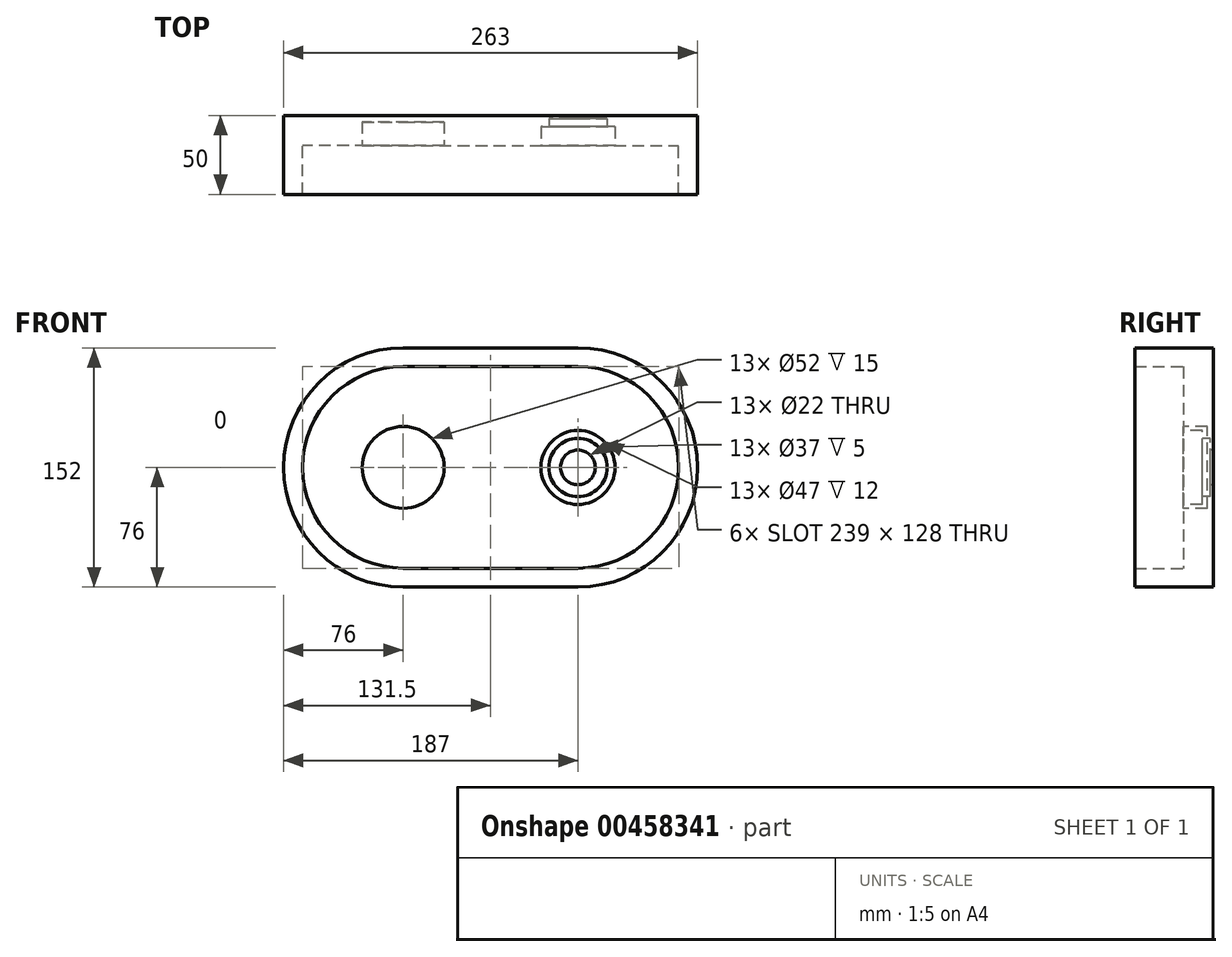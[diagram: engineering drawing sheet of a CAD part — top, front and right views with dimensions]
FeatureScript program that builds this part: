
annotation { "Feature Type Name" : "Feature", "Feature Type Description" : "" }
export const myFeature = defineFeature(function(context is Context, id is Id, definition is map)
    precondition{}
    {
        {
            var Q0;
            Q0=qCreatedBy(makeId("Front.planeOp"),FACE);
            var sketch = newSketch(context, id + "F0", { "sketchPlane" : qUnion([Q0])});
            skArc(sketch, "E0", {"start": v(0, 76) * mm, "mid": v(-76, 0) * mm, "end": v(0, -76) * mm});
            skArc(sketch, "E1", {"start": v(111, -76) * mm, "mid": v(187, 0) * mm, "end": v(111, 76) * mm});
            skLineSegment(sketch, "E2", {"start": v(0, 76) * mm, "end": v(111, 76) * mm});
            skLineSegment(sketch, "E3", {"start": v(0, -76) * mm, "end": v(111, -76) * mm});
            skSolve(sketch);
        }
        {
            var Q0;
            Q0=qCreatedBy(makeId("Front.planeOp"),FACE);
            cPlane(context, id + "F1", {"entities" : qUnion([Q0]), "cplaneType" : CPlaneType.OFFSET, "offset" : 19 * mm, "width" : 150 * mm, "height" : 150 * mm});
        }
        {
            var Q0;
            Q0=makeQuery(id+"F0.imprint","IMPRINT",FACE,{"disambiguationData":[TD([[makeQuery(id+"F0.imprint","IMPRINT",EDGE,{"derivedFrom":sQuery(id+"F0.wireOp",EDGE,"E0")}),1.0]])]});
            extrude(context, id + "F2", {"entities" : qUnion([Q0]), "depth" : 50 * mm, "offsetDistance" : 25 * mm});
        }
        {
            var Q0;
            Q0=qCreatedBy(id+"F1.planeOp",FACE);
            var sketch = newSketch(context, id + "F3", { "sketchPlane" : qUnion([Q0])});
            skArc(sketch, "E4", {"start": v(0, 64) * mm, "mid": v(-64, 0) * mm, "end": v(0, -64) * mm});
            skArc(sketch, "E5", {"start": v(111, -64) * mm, "mid": v(175, 0) * mm, "end": v(111, 64) * mm});
            skLineSegment(sketch, "E6", {"start": v(0, 64) * mm, "end": v(111, 64) * mm});
            skLineSegment(sketch, "E7", {"start": v(0, -64) * mm, "end": v(111, -64) * mm});
            skCircle(sketch, "E8", {"center": v(0, 0) * mm, "radius": 26 * mm});
            skSolve(sketch);
        }
        {
            var Q0;
            Q0 = qSketchRegion(id + "F3", true);
            extrude(context, id + "F4", {"entities" : qUnion([Q0]), "operationType" : NewBodyOperationType.REMOVE, "depth" : 100 * mm, "offsetDistance" : 25 * mm});
        }
        {
            var Q0;
            Q0=makeQuery(id+"F4.boolean.opBoolean","SPLIT",FACE,{"disambiguationData":[TD([makeQuery(id+"F4.opExtrude","SWEPT_FACE",FACE,{"disambiguationData":[OSD([sQuery(id+"F3.wireOp",EDGE,"E8")])]})])],"derivedFrom":makeQuery(id+"F2.opExtrude","CAP_FACE",FACE,{"disambiguationData":[OSD([sQuery(id+"F0.wireOp",EDGE,"E0"),sQuery(id+"F0.wireOp",EDGE,"E1"),sQuery(id+"F0.wireOp",EDGE,"E2"),sQuery(id+"F0.wireOp",EDGE,"E3")])],"isStart":false})});
            extrude(context, id + "F5", {"entities" : qUnion([Q0]), "operationType" : NewBodyOperationType.REMOVE, "oppositeDirection" : true, "depth" : 46 * mm, "offsetDistance" : 25 * mm});
        }
        {
            var Q0;
            Q0=qCreatedBy(makeId("Right.planeOp"),FACE);
            cPlane(context, id + "F6", {"entities" : qUnion([Q0]), "cplaneType" : CPlaneType.OFFSET, "offset" : 111 * mm, "width" : 150 * mm, "height" : 150 * mm});
        }
        {
            var Q0;
            Q0=qCreatedBy(id+"F6.planeOp",FACE);
            var sketch = newSketch(context, id + "F7", { "sketchPlane" : qUnion([Q0])});
            skLineSegment(sketch, "E9.bottom", {"start": v(0, 0) * mm, "end": v(-19, 0) * mm});
            skLineSegment(sketch, "E9.top", {"start": v(0, 11) * mm, "end": v(-2, 11) * mm});
            skLineSegment(sketch, "E9.left", {"start": v(0, 0) * mm, "end": v(0, 11) * mm});
            skLineSegment(sketch, "E9.right", {"start": v(-19, 0) * mm, "end": v(-19, 11) * mm});
            skLineSegment(sketch, "E10.bottom", {"start": v(-19, 0) * mm, "end": v(-7, 0) * mm});
            skLineSegment(sketch, "E10.top", {"start": v(-19, 23.5) * mm, "end": v(-7, 23.5) * mm});
            skLineSegment(sketch, "E10.left", {"start": v(-19, 0) * mm, "end": v(-19, 23.5) * mm});
            skLineSegment(sketch, "E10.right", {"start": v(-7, 18.5) * mm, "end": v(-7, 23.5) * mm});
            skLineSegment(sketch, "E11.bottom", {"start": v(-19, 0) * mm, "end": v(-2, 0) * mm});
            skLineSegment(sketch, "E11.top", {"start": v(-7, 18.5) * mm, "end": v(-2, 18.5) * mm});
            skLineSegment(sketch, "E11.left", {"start": v(-19, 0) * mm, "end": v(-19, 18.5) * mm});
            skLineSegment(sketch, "E11.right", {"start": v(-2, 11) * mm, "end": v(-2, 18.5) * mm});
            skLineSegment(sketch, "E12", {"start": v(-19, 0) * mm, "end": v(-75.36, 0) * mm, "construction": true});
            skSolve(sketch);
        }
        {
            var Q0;
            {var subQ0=sQuery(id+"F7.wireOp",EDGE,"E9.bottom");Q0=makeQuery(id+"F7.imprint","IMPRINT",FACE,{"disambiguationData":[TD([[makeQuery(id+"F7.imprint","IMPRINT",EDGE,{"derivedFrom":subQ0}),-1.0]])]});}
            var Q1;
            Q1=sQuery(id+"F7.wireOp",EDGE,"E12");
            revolve(context, id + "F8", {"operationType" : NewBodyOperationType.REMOVE, "entities" : qUnion([Q0]), "axis" : qUnion([Q1]), "revolveType" : RevolveType.FULL, "oppositeDirection" : true});
        }
    });
